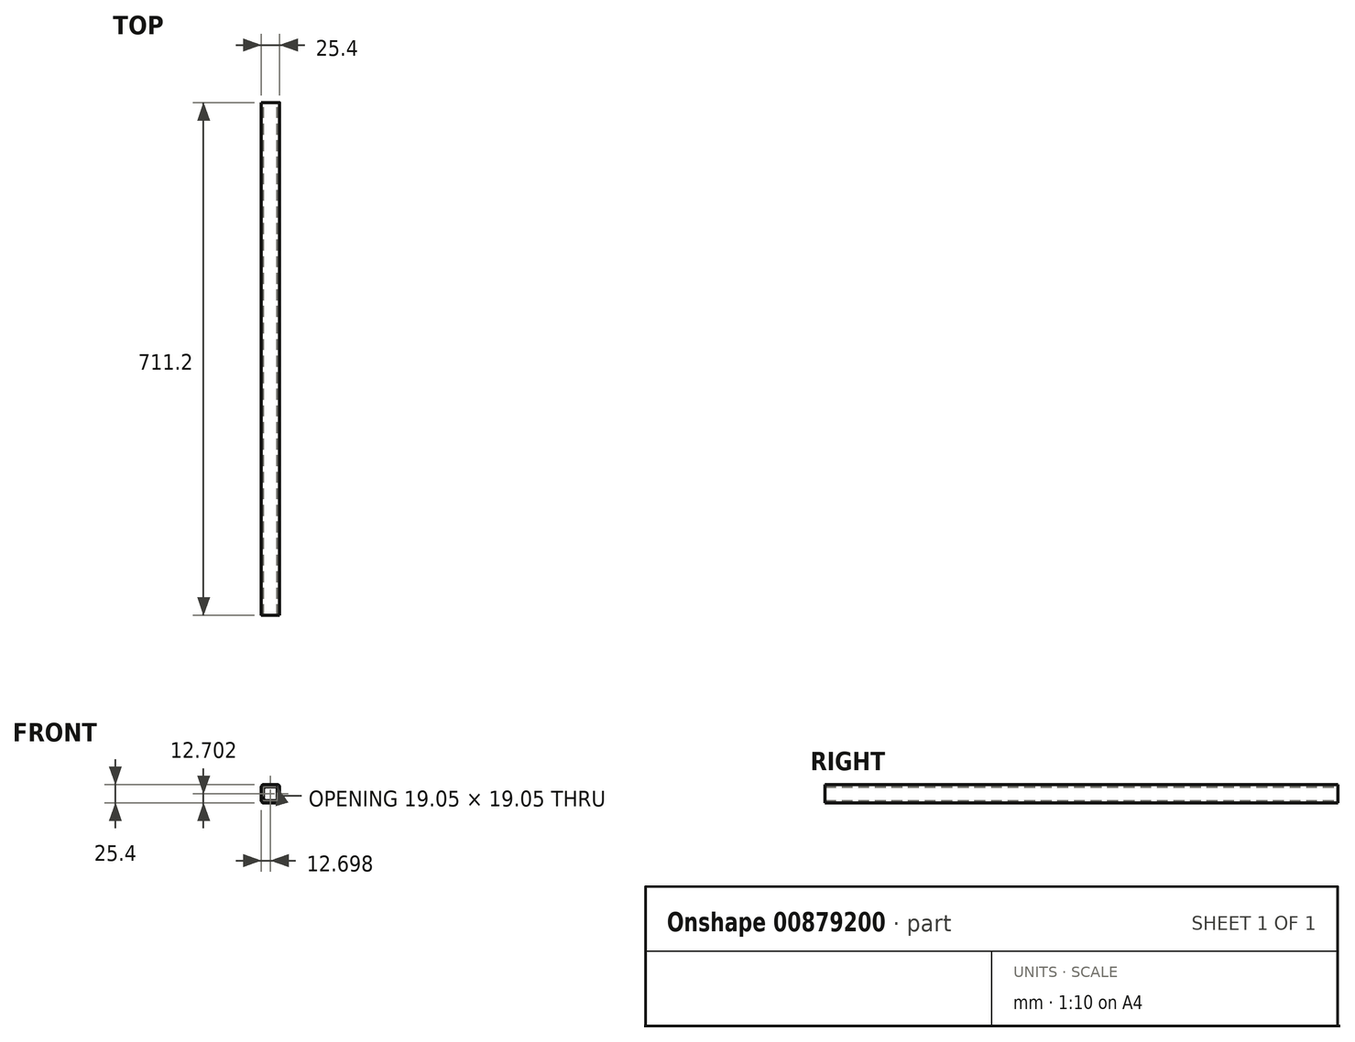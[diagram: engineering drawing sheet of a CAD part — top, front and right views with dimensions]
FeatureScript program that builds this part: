
annotation { "Feature Type Name" : "Feature", "Feature Type Description" : "" }
export const myFeature = defineFeature(function(context is Context, id is Id, definition is map)
    precondition{}
    {
        {
            var Q0;
            Q0=qCreatedBy(makeId("Front.planeOp"),FACE);
            var sketch = newSketch(context, id + "F0", { "sketchPlane" : qUnion([Q0])});
            skLineSegment(sketch, "E0.bottom", {"start": v(8.82, -13.08) * mm, "end": v(-10.23, -13.08) * mm});
            skLineSegment(sketch, "E0.top", {"start": v(8.82, 12.32) * mm, "end": v(-10.23, 12.32) * mm});
            skLineSegment(sketch, "E0.left", {"start": v(12, -9.9) * mm, "end": v(12, 9.15) * mm});
            skLineSegment(sketch, "E0.right", {"start": v(-13.4, -9.9) * mm, "end": v(-13.4, 9.15) * mm});
            skLineSegment(sketch, "E1.bottom", {"start": v(5.65, -9.9) * mm, "end": v(-7.05, -9.9) * mm});
            skLineSegment(sketch, "E1.top", {"start": v(5.65, 9.15) * mm, "end": v(-7.05, 9.15) * mm});
            skLineSegment(sketch, "E1.left", {"start": v(8.82, -6.73) * mm, "end": v(8.82, 5.97) * mm});
            skLineSegment(sketch, "E1.right", {"start": v(-10.23, -6.73) * mm, "end": v(-10.23, 5.97) * mm});
            skPoint(sketch, "E2.visualSharp", {"position": v(8.82, 9.15) * mm});
            skArc(sketch, "E2.filletArc", {"start": v(8.82, 5.97) * mm, "mid": v(7.9, 8.22) * mm, "end": v(5.65, 9.15) * mm});
            skPoint(sketch, "E3.visualSharp", {"position": v(-10.23, 9.15) * mm});
            skArc(sketch, "E3.filletArc", {"start": v(-7.05, 9.15) * mm, "mid": v(-9.3, 8.22) * mm, "end": v(-10.23, 5.97) * mm});
            skPoint(sketch, "E4.visualSharp", {"position": v(-10.23, -9.9) * mm});
            skArc(sketch, "E4.filletArc", {"start": v(-10.23, -6.73) * mm, "mid": v(-9.3, -8.97) * mm, "end": v(-7.05, -9.9) * mm});
            skPoint(sketch, "E5.visualSharp", {"position": v(8.82, -9.9) * mm});
            skArc(sketch, "E5.filletArc", {"start": v(5.65, -9.9) * mm, "mid": v(7.9, -8.97) * mm, "end": v(8.82, -6.73) * mm});
            skPoint(sketch, "E6.visualSharp", {"position": v(12, 12.32) * mm});
            skArc(sketch, "E6.filletArc", {"start": v(12, 9.15) * mm, "mid": v(11.07, 11.4) * mm, "end": v(8.82, 12.32) * mm});
            skPoint(sketch, "E7.visualSharp", {"position": v(-13.4, 12.32) * mm});
            skArc(sketch, "E7.filletArc", {"start": v(-10.23, 12.32) * mm, "mid": v(-12.47, 11.4) * mm, "end": v(-13.4, 9.15) * mm});
            skPoint(sketch, "E8.visualSharp", {"position": v(-13.4, -13.08) * mm});
            skArc(sketch, "E8.filletArc", {"start": v(-13.4, -9.9) * mm, "mid": v(-12.47, -12.15) * mm, "end": v(-10.23, -13.08) * mm});
            skPoint(sketch, "E9.visualSharp", {"position": v(12, -13.08) * mm});
            skArc(sketch, "E9.filletArc", {"start": v(8.82, -13.08) * mm, "mid": v(11.07, -12.15) * mm, "end": v(12, -9.9) * mm});
            skSolve(sketch);
        }
        {
            var Q0;
            Q0=qSketchRegion(id+"F0",true);
            extrude(context, id + "F1", {"entities" : qUnion([Q0]), "depth" : 711.2 * mm, "offsetDistance" : 25.4 * mm});
        }
    });
